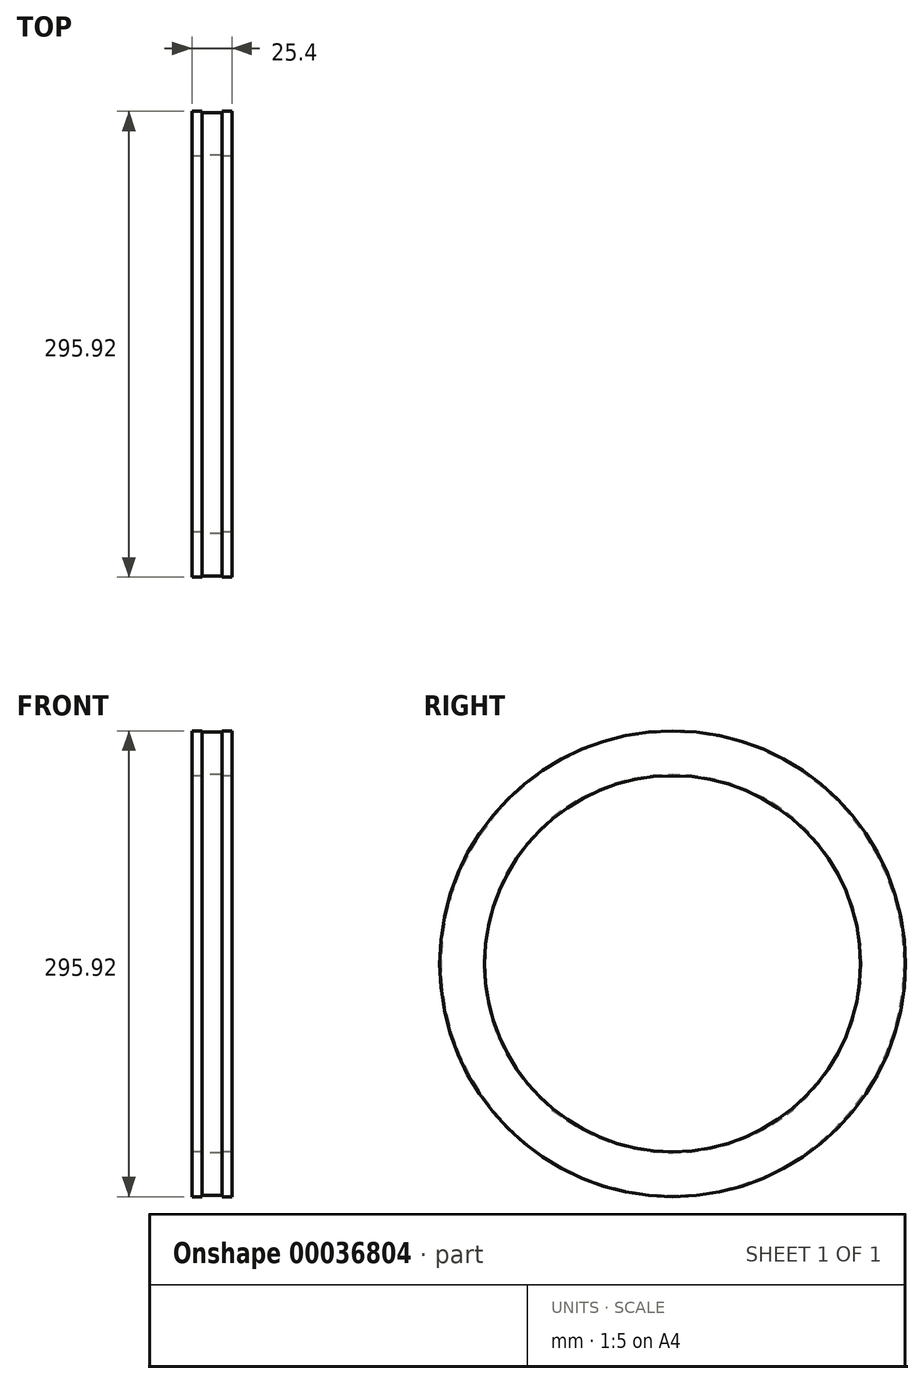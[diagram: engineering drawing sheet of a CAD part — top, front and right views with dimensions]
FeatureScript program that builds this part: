
annotation { "Feature Type Name" : "Feature", "Feature Type Description" : "" }
export const myFeature = defineFeature(function(context is Context, id is Id, definition is map)
    precondition{}
    {
        {
            var Q0;
            Q0=qCreatedBy(makeId("Front.planeOp"),FACE);
            var sketch = newSketch(context, id + "F0", { "sketchPlane" : qUnion([Q0])});
            skLineSegment(sketch, "E0", {"start": v(0, 147.96) * mm, "end": v(6.35, 147.96) * mm});
            skLineSegment(sketch, "E1", {"start": v(6.35, 147.96) * mm, "end": v(6.35, 147.2) * mm});
            skLineSegment(sketch, "E2", {"start": v(6.35, 147.2) * mm, "end": v(19.05, 147.2) * mm});
            skLineSegment(sketch, "E3", {"start": v(19.05, 147.2) * mm, "end": v(19.05, 147.96) * mm});
            skLineSegment(sketch, "E4", {"start": v(19.05, 147.96) * mm, "end": v(25.4, 147.96) * mm});
            skLineSegment(sketch, "E5", {"start": v(25.4, 147.96) * mm, "end": v(25.4, 119.38) * mm});
            skLineSegment(sketch, "E6", {"start": v(25.4, 119.38) * mm, "end": v(19.05, 119.38) * mm});
            skLineSegment(sketch, "E7", {"start": v(19.05, 119.38) * mm, "end": v(19.05, 120.14) * mm});
            skLineSegment(sketch, "E8", {"start": v(19.05, 120.14) * mm, "end": v(6.35, 120.14) * mm});
            skLineSegment(sketch, "E9", {"start": v(6.35, 120.14) * mm, "end": v(6.35, 119.38) * mm});
            skLineSegment(sketch, "E10", {"start": v(6.35, 119.38) * mm, "end": v(0, 119.38) * mm});
            skLineSegment(sketch, "E11", {"start": v(0, 119.38) * mm, "end": v(0, 147.96) * mm});
            skLineSegment(sketch, "E12", {"start": v(-4.85, 0) * mm, "end": v(5.05, 0) * mm});
            skSolve(sketch);
        }
        {
            var Q0;
            Q0=makeQuery(id+"F0.imprint","IMPRINT",FACE,{"disambiguationData":[TD([[makeQuery(id+"F0.imprint","IMPRINT",EDGE,{"derivedFrom":sQuery(id+"F0.wireOp",EDGE,"E0")}),-1.0]])]});
            var Q1;
            Q1=sQuery(id+"F0.wireOp",EDGE,"E12");
            revolve(context, id + "F1", {"entities" : qUnion([Q0]), "axis" : qUnion([Q1]), "revolveType" : RevolveType.FULL});
        }
    });
